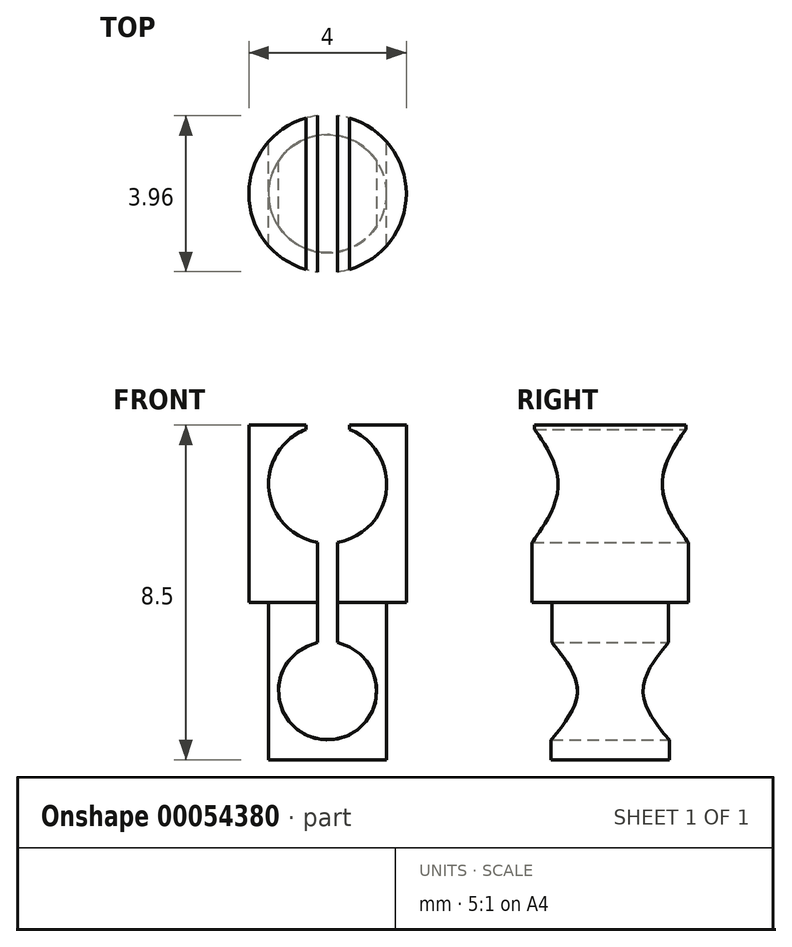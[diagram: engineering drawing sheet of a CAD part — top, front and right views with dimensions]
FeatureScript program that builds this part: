
annotation { "Feature Type Name" : "Feature", "Feature Type Description" : "" }
export const myFeature = defineFeature(function(context is Context, id is Id, definition is map)
    precondition{}
    {
        {
            var Q0;
            Q0=qCreatedBy(makeId("Top.planeOp"),FACE);
            var sketch = newSketch(context, id + "F0", { "sketchPlane" : qUnion([Q0])});
            skCircle(sketch, "E0", {"center": v(0, 0) * mm, "radius": 1.5 * mm});
            skCircle(sketch, "E1", {"center": v(0, 0) * mm, "radius": 2 * mm});
            skSolve(sketch);
        }
        {
            var Q0;
            Q0=makeQuery(id+"F0.imprint","IMPRINT",FACE,{"disambiguationData":[TD([[makeQuery(id+"F0.imprint","IMPRINT",EDGE,{"derivedFrom":sQuery(id+"F0.wireOp",EDGE,"E0")}),1.0]])]});
            var Q1;
            Q1=sQuery(id+"F0.wireOp",EDGE,"E0");
            extrude(context, id + "F1", {"entities" : qUnion([Q0]), "surfaceEntities" : qUnion([Q1]), "oppositeDirection" : true, "depth" : 4 * mm, "offsetDistance" : 25 * mm});
        }
        {
            var Q0;
            Q0=makeQuery(id+"F0.imprint","IMPRINT",FACE,{"disambiguationData":[TD([[makeQuery(id+"F0.imprint","IMPRINT",EDGE,{"derivedFrom":sQuery(id+"F0.wireOp",EDGE,"E0")}),1.0]])]});
            var Q1;
            Q1=makeQuery(id+"F0.imprint","IMPRINT",FACE,{"disambiguationData":[TD([[makeQuery(id+"F0.imprint","IMPRINT",EDGE,{"derivedFrom":sQuery(id+"F0.wireOp",EDGE,"E0")}),-1.0]])]});
            var Q2;
            Q2=sQuery(id+"F0.wireOp",EDGE,"E1");
            extrude(context, id + "F2", {"entities" : qUnion([Q0, Q1]), "operationType" : NewBodyOperationType.ADD, "surfaceEntities" : qUnion([Q2]), "depth" : 4.5 * mm, "offsetDistance" : 25 * mm});
        }
        {
            var Q0;
            Q0=qCreatedBy(makeId("Front.planeOp"),FACE);
            var sketch = newSketch(context, id + "F3", { "sketchPlane" : qUnion([Q0])});
            skCircle(sketch, "E2", {"center": v(0, 3) * mm, "radius": 1.5 * mm});
            skCircle(sketch, "E3", {"center": v(0, -2.25) * mm, "radius": 1.25 * mm});
            skLineSegment(sketch, "E4.bottom", {"start": v(-0.55, 4.5) * mm, "end": v(0.55, 4.5) * mm});
            skLineSegment(sketch, "E4.top", {"start": v(-0.55, 4.4) * mm, "end": v(0.55, 4.4) * mm});
            skLineSegment(sketch, "E4.left", {"start": v(-0.55, 4.5) * mm, "end": v(-0.55, 4.4) * mm});
            skLineSegment(sketch, "E4.right", {"start": v(0.55, 4.5) * mm, "end": v(0.55, 4.4) * mm});
            skLineSegment(sketch, "E5.bottom", {"start": v(-0.25, 1.52) * mm, "end": v(0.25, 1.52) * mm});
            skLineSegment(sketch, "E5.top", {"start": v(-0.25, -1.03) * mm, "end": v(0.25, -1.03) * mm});
            skLineSegment(sketch, "E5.left", {"start": v(-0.25, 1.52) * mm, "end": v(-0.25, -1.03) * mm});
            skLineSegment(sketch, "E5.right", {"start": v(0.25, 1.52) * mm, "end": v(0.25, -1.03) * mm});
            skSolve(sketch);
        }
        {
            var Q0;
            Q0 = qSketchRegion(id + "F3", true);
            var Q1;
            Q1=sQuery(id+"F3.wireOp",EDGE,"E2");
            extrude(context, id + "F4", {"entities" : qUnion([Q0]), "operationType" : NewBodyOperationType.REMOVE, "surfaceEntities" : qUnion([Q1]), "endBound" : BoundingType.SYMMETRIC, "depth" : 5 * mm, "offsetDistance" : 25 * mm});
        }
    });
